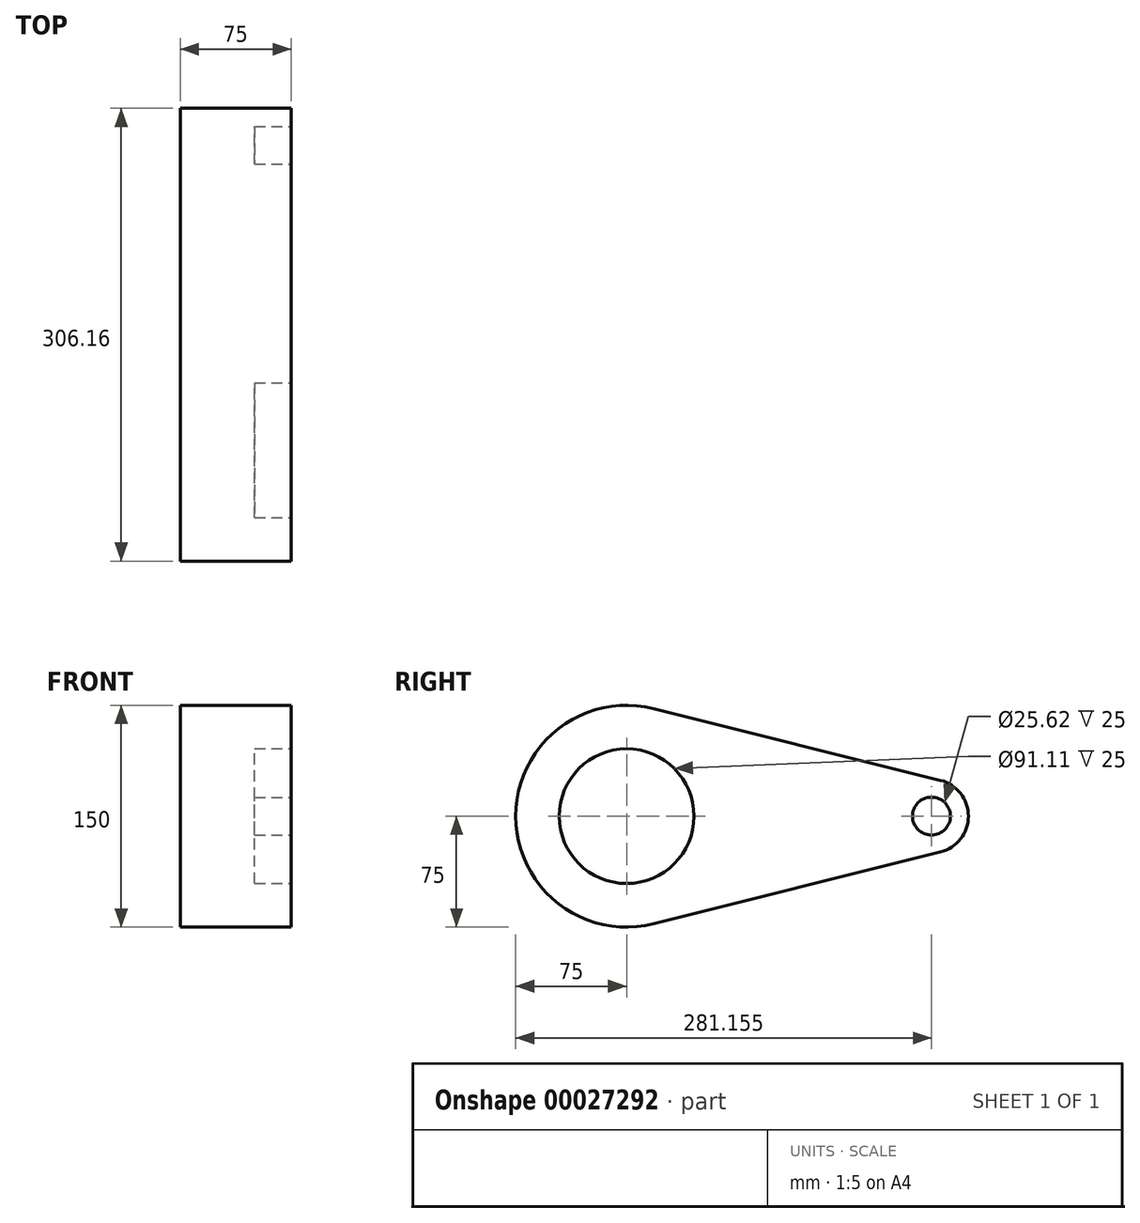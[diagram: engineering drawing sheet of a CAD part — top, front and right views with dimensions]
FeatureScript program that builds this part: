
annotation { "Feature Type Name" : "Feature", "Feature Type Description" : "" }
export const myFeature = defineFeature(function(context is Context, id is Id, definition is map)
    precondition{}
    {
        {
            var Q0;
            Q0=qCreatedBy(makeId("Right.planeOp"),FACE);
            var sketch = newSketch(context, id + "F0", { "sketchPlane" : qUnion([Q0])});
            skCircle(sketch, "E0", {"center": v(0, 0) * mm, "radius": 75 * mm});
            skCircle(sketch, "E1", {"center": v(206.16, 0) * mm, "radius": 25 * mm});
            skLineSegment(sketch, "E2", {"start": v(18.2, 72.76) * mm, "end": v(212.22, 24.25) * mm});
            skLineSegment(sketch, "E3", {"start": v(18.2, -72.76) * mm, "end": v(212.22, -24.25) * mm});
            skSolve(sketch);
        }
        {
            var Q0;
            {var subQ0=sQuery(id+"F0.wireOp",EDGE,"E0");var subQ2=makeQuery(id+"F0.imprint","INTERSECT",VERTEX,{"derivedFrom":[subQ0,sQuery(id+"F0.wireOp",EDGE,"E2")]});Q0=makeQuery(id+"F0.imprint","IMPRINT",FACE,{"disambiguationData":[TD([[makeQuery(id+"F0.imprint","IMPRINT",EDGE,{"disambiguationData":[TD([[subQ2,-1.0]])],"derivedFrom":subQ0}),1.0]])]});}
            var Q1;
            {var subQ1=sQuery(id+"F0.wireOp",EDGE,"E2");Q1=makeQuery(id+"F0.imprint","IMPRINT",FACE,{"disambiguationData":[TD([[makeQuery(id+"F0.imprint","IMPRINT",EDGE,{"derivedFrom":subQ1}),-1.0]])]});}
            var Q2;
            {var subQ0=sQuery(id+"F0.wireOp",EDGE,"E1");var subQ2=makeQuery(id+"F0.imprint","INTERSECT",VERTEX,{"derivedFrom":[subQ0,sQuery(id+"F0.wireOp",EDGE,"E2")]});Q2=makeQuery(id+"F0.imprint","IMPRINT",FACE,{"disambiguationData":[TD([[makeQuery(id+"F0.imprint","IMPRINT",EDGE,{"disambiguationData":[TD([[subQ2,-1.0]])],"derivedFrom":subQ0}),1.0]])]});}
            extrude(context, id + "F1", {"entities" : qUnion([Q0, Q1, Q2]), "depth" : 75 * mm});
        }
        {
            var Q0;
            Q0=makeQuery(id+"F1.opExtrude","CAP_FACE",FACE,{"disambiguationData":[OSD([sQuery(id+"F0.wireOp",EDGE,"E0"),sQuery(id+"F0.wireOp",EDGE,"E1"),sQuery(id+"F0.wireOp",EDGE,"E2"),sQuery(id+"F0.wireOp",EDGE,"E3")])],"isStart":false});
            var sketch = newSketch(context, id + "F2", { "sketchPlane" : qUnion([Q0])});
            skCircle(sketch, "E4", {"center": v(206.16, 0) * mm, "radius": 12.8 * mm});
            skCircle(sketch, "E5", {"center": v(0, 0) * mm, "radius": 45.56 * mm});
            skSolve(sketch);
        }
        {
            var Q0;
            Q0=makeQuery(id+"F2.imprint","IMPRINT",FACE,{"disambiguationData":[TD([[makeQuery(id+"F2.imprint","IMPRINT",EDGE,{"derivedFrom":sQuery(id+"F2.wireOp",EDGE,"E5")}),1.0]])]});
            var Q1;
            Q1=makeQuery(id+"F2.imprint","IMPRINT",FACE,{"disambiguationData":[TD([[makeQuery(id+"F2.imprint","IMPRINT",EDGE,{"derivedFrom":sQuery(id+"F2.wireOp",EDGE,"E4")}),1.0]])]});
            var Q2;
            Q2=sQuery(id+"F2.wireOp",EDGE,"E5");
            var Q3;
            Q3=sQuery(id+"F2.wireOp",EDGE,"E4");
            extrude(context, id + "F3", {"entities" : qUnion([Q0, Q1]), "operationType" : NewBodyOperationType.REMOVE, "surfaceEntities" : qUnion([Q2, Q3]), "oppositeDirection" : true, "depth" : 25 * mm});
        }
    });
